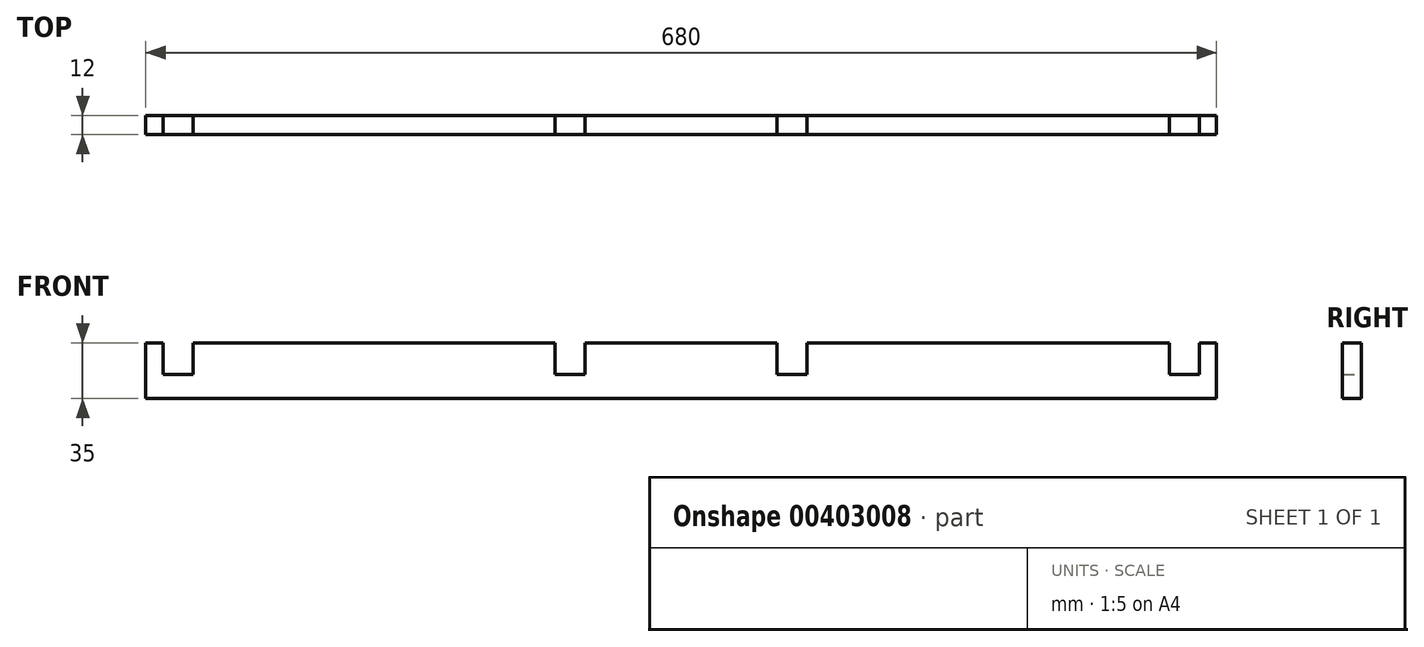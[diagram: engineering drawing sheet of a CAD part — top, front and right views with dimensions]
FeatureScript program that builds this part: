
annotation { "Feature Type Name" : "Feature", "Feature Type Description" : "" }
export const myFeature = defineFeature(function(context is Context, id is Id, definition is map)
    precondition{}
    {
        {
            var Q0;
            Q0=qCreatedBy(makeId("Front.planeOp"),FACE);
            var sketch = newSketch(context, id + "F0", { "sketchPlane" : qUnion([Q0])});
            skLineSegment(sketch, "E0.bottom", {"start": v(0, 0) * mm, "end": v(680, 0) * mm});
            skLineSegment(sketch, "E0.top", {"start": v(0, 35) * mm, "end": v(11, 35) * mm});
            skLineSegment(sketch, "E0.left", {"start": v(0, 0) * mm, "end": v(0, 35) * mm});
            skLineSegment(sketch, "E0.right", {"start": v(680, 0) * mm, "end": v(680, 35) * mm});
            skLineSegment(sketch, "E1.top", {"start": v(11, 15) * mm, "end": v(30, 15) * mm});
            skLineSegment(sketch, "E1.left", {"start": v(11, 35) * mm, "end": v(11, 15) * mm});
            skLineSegment(sketch, "E1.right", {"start": v(30, 35) * mm, "end": v(30, 15) * mm});
            skLineSegment(sketch, "E2.top", {"start": v(650, 15) * mm, "end": v(669, 15) * mm});
            skLineSegment(sketch, "E2.left", {"start": v(650, 35) * mm, "end": v(650, 15) * mm});
            skLineSegment(sketch, "E2.right", {"start": v(669, 35) * mm, "end": v(669, 15) * mm});
            skLineSegment(sketch, "E3.trimOffspring", {"start": v(30, 35) * mm, "end": v(260, 35) * mm});
            skLineSegment(sketch, "E4.trimOffspring", {"start": v(669, 35) * mm, "end": v(680, 35) * mm});
            skLineSegment(sketch, "E5.top", {"start": v(260, 15) * mm, "end": v(279, 15) * mm});
            skLineSegment(sketch, "E5.left", {"start": v(260, 35) * mm, "end": v(260, 15) * mm});
            skLineSegment(sketch, "E5.right", {"start": v(279, 35) * mm, "end": v(279, 15) * mm});
            skLineSegment(sketch, "E6.trimOffspring", {"start": v(279, 35) * mm, "end": v(401, 35) * mm});
            skLineSegment(sketch, "E7.top", {"start": v(401, 15) * mm, "end": v(420, 15) * mm});
            skLineSegment(sketch, "E7.left", {"start": v(401, 35) * mm, "end": v(401, 15) * mm});
            skLineSegment(sketch, "E7.right", {"start": v(420, 35) * mm, "end": v(420, 15) * mm});
            skLineSegment(sketch, "E8.trimOffspring", {"start": v(420, 35) * mm, "end": v(650, 35) * mm});
            skSolve(sketch);
        }
        {
            var Q0;
            Q0=makeQuery(id+"F0.imprint","IMPRINT",FACE,{"disambiguationData":[TD([[makeQuery(id+"F0.imprint","IMPRINT",EDGE,{"derivedFrom":sQuery(id+"F0.wireOp",EDGE,"ESCJjQW9-Kipg-MWqb-1C1w-8BTgatxLSc3F.bottom")}),1.0]])]});
            var Q1;
            Q1=makeQuery(id+"F0.imprint","IMPRINT",FACE,{"disambiguationData":[TD([[makeQuery(id+"F0.imprint","IMPRINT",EDGE,{"derivedFrom":sQuery(id+"F0.wireOp",EDGE,"E0.bottom")}),1.0]])]});
            extrude(context, id + "F1", {"entities" : qUnion([Q0, Q1]), "depth" : 12 * mm});
        }
    });
